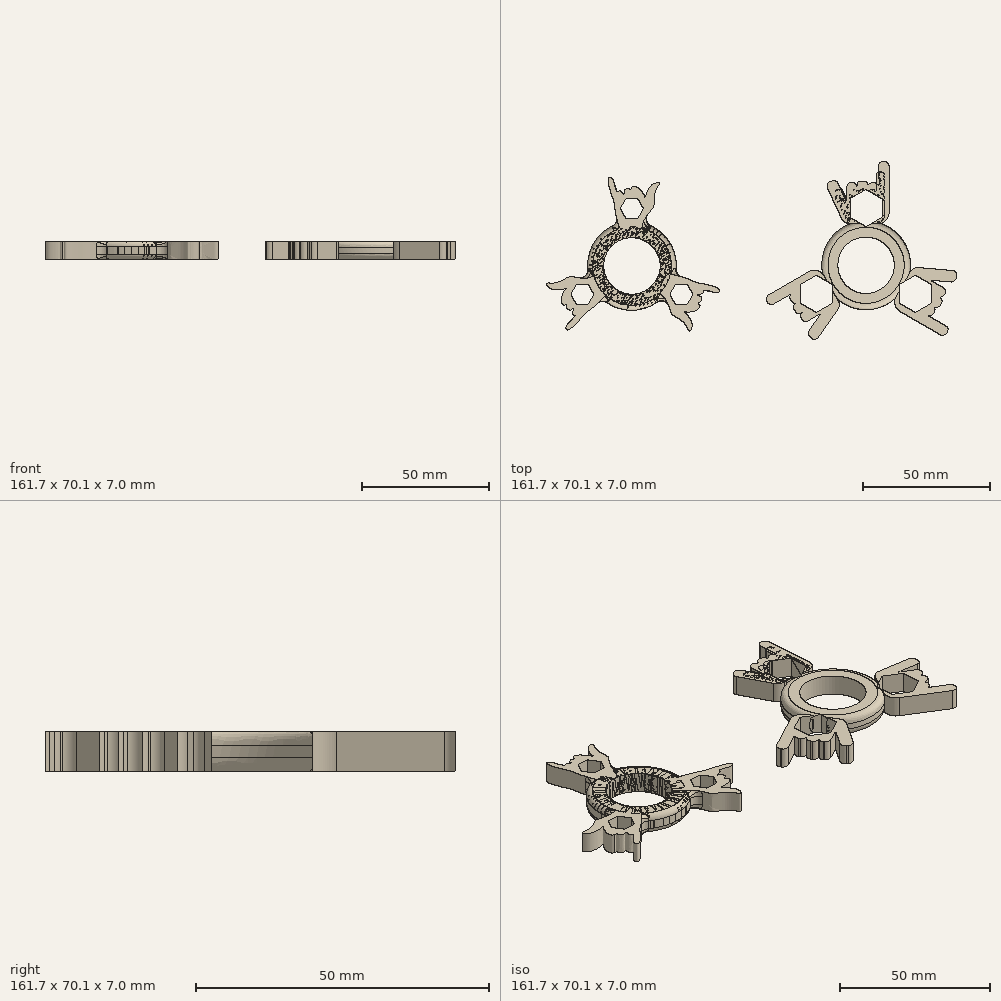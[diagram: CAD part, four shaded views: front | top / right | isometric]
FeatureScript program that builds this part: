
annotation { "Feature Type Name" : "Feature", "Feature Type Description" : "" }
export const myFeature = defineFeature(function(context is Context, id is Id, definition is map)
    precondition{}
    {
        {
            var Q0;
            Q0=qCreatedBy(makeId("Top.planeOp"),FACE);
            var sketch = newSketch(context, id + "F0", { "sketchPlane" : qUnion([Q0])});
            skPoint(sketch, "E0", {"position": v(0, 14) * mm});
            skPoint(sketch, "E1", {"position": v(0, 11.12) * mm});
            skLineSegment(sketch, "E2", {"start": v(-11.75, 14) * mm, "end": v(11.75, 14) * mm});
            skLineSegment(sketch, "E3", {"start": v(0, 14) * mm, "end": v(11.75, 14) * mm});
            skLineSegment(sketch, "E4", {"start": v(-11.75, 14) * mm, "end": v(0, 14) * mm});
            skLineSegment(sketch, "E5", {"start": v(0, 0) * mm, "end": v(0, 40) * mm});
            skPoint(sketch, "E6.13.internal.snap0", {"position": v(5.87, 14) * mm});
            skFitSpline(sketch, "E6", {"points": [v(5.87, 14) * mm, v(4.83, 16.75) * mm, v(4.45, 19.91) * mm, v(7.38, 24.48) * mm, v(8.56, 26.16) * mm, v(8.76, 28.18) * mm, v(8.91, 30.79) * mm, v(9.87, 33.45) * mm, v(10.71, 34.83) * mm, v(10.77, 35.56) * mm, v(9.34, 35.54) * mm, v(7.98, 34.9) * mm, v(6.44, 32.88) * mm, v(5.87, 31.7) * mm, v(5.72, 31.37) * mm, v(5.26, 29.43) * mm, v(4.97, 30.58) * mm, v(3.64, 32.5) * mm, v(2.81, 33.48) * mm, v(1.13, 34.27) * mm, v(0.25, 34) * mm, v(-0.2, 33.59) * mm, v(-0.3, 32.84) * mm, v(-1.06, 33.34) * mm, v(-2.25, 33.15) * mm, v(-3.12, 32.31) * mm, v(-3, 31.03) * mm, v(-4.48, 32.43) * mm, v(-5.19, 32.37) * mm, v(-5.55, 32.22) * mm, v(-5.81, 31.95) * mm, v(-6.05, 32.54) * mm, v(-6.77, 34.35) * mm, v(-7.78, 37.38) * mm, v(-9.18, 37.45) * mm, v(-9.22, 34.9) * mm, v(-9.22, 34.9) * mm, v(-8.3, 31.7) * mm, v(-7.12, 28.19) * mm, v(-6.67, 24.78) * mm, v(-6.18, 22.23) * mm, v(-5.26, 19) * mm, v(-4.33, 17.17) * mm, v(-3.58, 15.28) * mm, v(-3.38, 13.9) * mm, v(-3.35, 14) * mm], "startDerivative": vector(-16.05, 41.1) * mm, "endDerivative": vector(-65.23, -174.75) * mm});
            skLineSegment(sketch, "E7", {"start": v(0, 40) * mm, "end": v(-11.75, 40) * mm});
            skLineSegment(sketch, "E8", {"start": v(-11.75, 40) * mm, "end": v(-11.75, 45.72) * mm});
            skPoint(sketch, "E9", {"position": v(-3.55, 14) * mm});
            skLineSegment(sketch, "E10", {"start": v(0, 14) * mm, "end": v(0, -8.25) * mm});
            skCircle(sketch, "E11", {"center": v(0, 2.87) * mm, "radius": 11.13 * mm});
            skCircle(sketch, "E12", {"center": v(0, 2.87) * mm, "radius": 17.5 * mm});
            skCircle(sketch, "E13.cCircle", {"center": v(0, 25.42) * mm, "radius": 3.97 * mm, "construction": true});
            skLineSegment(sketch, "E13.0", {"start": v(2.3, 21.45) * mm, "end": v(-2.3, 21.45) * mm});
            skLineSegment(sketch, "E13.1", {"start": v(-2.3, 21.45) * mm, "end": v(-4.58, 25.42) * mm});
            skLineSegment(sketch, "E13.2", {"start": v(-4.58, 25.42) * mm, "end": v(-2.3, 29.4) * mm});
            skLineSegment(sketch, "E13.3", {"start": v(-2.3, 29.4) * mm, "end": v(2.3, 29.4) * mm});
            skLineSegment(sketch, "E13.4", {"start": v(2.3, 29.4) * mm, "end": v(4.58, 25.42) * mm});
            skLineSegment(sketch, "E13.5", {"start": v(4.58, 25.42) * mm, "end": v(2.3, 21.45) * mm});
            skPoint(sketch, "E13.0.midPoint", {"position": v(0, 21.45) * mm});
            skLineSegment(sketch, "E14", {"start": v(0, 2.87) * mm, "end": v(-3.26, 2.87) * mm});
            skSolve(sketch);
        }
        {
            var Q0;
            Q0 = qSketchRegion(id + "F0", true);
            extrude(context, id + "F1", {"entities" : qUnion([Q0]), "depth" : 7 * mm, "offsetDistance" : 25 * mm});
        }
        {
            var Q0;
            Q0=qCreatedBy(makeId("Top.planeOp"),FACE);
            var sketch = newSketch(context, id + "F2", { "sketchPlane" : qUnion([Q0])});
            skPoint(sketch, "E15", {"position": v(92.33, 14.59) * mm});
            skLineSegment(sketch, "E16", {"start": v(92.33, 0.24) * mm, "end": v(92.33, 40.24) * mm});
            skLineSegment(sketch, "E17", {"start": v(92.33, 40.24) * mm, "end": v(80.58, 40.24) * mm});
            skLineSegment(sketch, "E18", {"start": v(80.58, 40.24) * mm, "end": v(80.58, 45.96) * mm});
            skLineSegment(sketch, "E19", {"start": v(92.33, 14.59) * mm, "end": v(92.33, -8.35) * mm});
            skCircle(sketch, "E20", {"center": v(92.33, 3.12) * mm, "radius": 11.13 * mm});
            skCircle(sketch, "E21", {"center": v(92.33, 3.12) * mm, "radius": 17.5 * mm});
            skCircle(sketch, "E22.cCircle", {"center": v(91.53, 25.67) * mm, "radius": 3.97 * mm, "construction": true});
            skPoint(sketch, "E22.0.midPoint", {"position": v(91.53, 21.7) * mm});
            skLineSegment(sketch, "E23.bottom", {"start": v(87.38, 33.03) * mm, "end": v(87.71, 33.03) * mm});
            skLineSegment(sketch, "E23.top", {"start": v(87.38, 24.01) * mm, "end": v(87.71, 24.01) * mm});
            skLineSegment(sketch, "E23.left", {"start": v(85.88, 31.53) * mm, "end": v(85.88, 25.51) * mm});
            skLineSegment(sketch, "E23.right", {"start": v(89.21, 31.53) * mm, "end": v(89.21, 25.51) * mm});
            skLineSegment(sketch, "E24.bottom", {"start": v(94.82, 33.03) * mm, "end": v(94.4, 33.03) * mm});
            skLineSegment(sketch, "E24.top", {"start": v(94.82, 24.53) * mm, "end": v(94.4, 24.53) * mm});
            skLineSegment(sketch, "E24.left", {"start": v(96.32, 31.53) * mm, "end": v(96.32, 26.03) * mm});
            skLineSegment(sketch, "E24.right", {"start": v(92.9, 31.53) * mm, "end": v(92.9, 26.03) * mm});
            skLineSegment(sketch, "E25", {"start": v(89.21, 32.08) * mm, "end": v(89.21, 33.03) * mm});
            skLineSegment(sketch, "E26", {"start": v(90.71, 33.58) * mm, "end": v(91.4, 33.58) * mm});
            skLineSegment(sketch, "E27", {"start": v(92.9, 33.03) * mm, "end": v(92.9, 32.08) * mm});
            skLineSegment(sketch, "E28", {"start": v(89.21, 24.18) * mm, "end": v(89.21, 24.01) * mm});
            skLineSegment(sketch, "E29", {"start": v(90.71, 22.68) * mm, "end": v(91.4, 22.68) * mm});
            skLineSegment(sketch, "E30", {"start": v(92.9, 24.18) * mm, "end": v(92.9, 24.53) * mm});
            skPoint(sketch, "E31.visualSharp", {"position": v(85.88, 24.01) * mm});
            skArc(sketch, "E31.filletArc", {"start": v(85.88, 25.51) * mm, "mid": v(86.32, 24.45) * mm, "end": v(87.38, 24.01) * mm});
            skPoint(sketch, "E32.visualSharp", {"position": v(89.21, 24.01) * mm});
            skArc(sketch, "E32.filletArc", {"start": v(87.71, 24.01) * mm, "mid": v(88.77, 24.45) * mm, "end": v(89.21, 25.51) * mm});
            skLineSegment(sketch, "E33", {"start": v(89.21, 24.01) * mm, "end": v(89.21, 25.51) * mm});
            skPoint(sketch, "E34.visualSharp", {"position": v(89.21, 22.68) * mm});
            skArc(sketch, "E34.filletArc", {"start": v(89.21, 24.18) * mm, "mid": v(89.65, 23.12) * mm, "end": v(90.71, 22.68) * mm});
            skPoint(sketch, "E35.visualSharp", {"position": v(92.9, 22.68) * mm});
            skArc(sketch, "E35.filletArc", {"start": v(91.4, 22.68) * mm, "mid": v(92.45, 23.12) * mm, "end": v(92.9, 24.18) * mm});
            skPoint(sketch, "E36.visualSharp", {"position": v(96.32, 24.53) * mm});
            skArc(sketch, "E36.filletArc", {"start": v(94.82, 24.53) * mm, "mid": v(95.88, 24.97) * mm, "end": v(96.32, 26.03) * mm});
            skPoint(sketch, "E37.visualSharp", {"position": v(96.32, 33.03) * mm});
            skArc(sketch, "E37.filletArc", {"start": v(96.32, 31.53) * mm, "mid": v(95.88, 32.6) * mm, "end": v(94.82, 33.03) * mm});
            skPoint(sketch, "E38.visualSharp", {"position": v(85.88, 33.03) * mm});
            skArc(sketch, "E38.filletArc", {"start": v(87.38, 33.03) * mm, "mid": v(86.32, 32.6) * mm, "end": v(85.88, 31.53) * mm});
            skPoint(sketch, "E39.visualSharp", {"position": v(89.21, 33.58) * mm});
            skArc(sketch, "E39.filletArc", {"start": v(90.71, 33.58) * mm, "mid": v(89.65, 33.14) * mm, "end": v(89.21, 32.08) * mm});
            skPoint(sketch, "E40.visualSharp", {"position": v(92.9, 33.58) * mm});
            skArc(sketch, "E40.filletArc", {"start": v(92.9, 32.08) * mm, "mid": v(92.45, 33.14) * mm, "end": v(91.4, 33.58) * mm});
            skPoint(sketch, "E41.visualSharp", {"position": v(92.9, 33.03) * mm});
            skArc(sketch, "E41.filletArc", {"start": v(94.4, 33.03) * mm, "mid": v(93.33, 32.6) * mm, "end": v(92.9, 31.53) * mm});
            skPoint(sketch, "E42.visualSharp", {"position": v(92.9, 24.53) * mm});
            skArc(sketch, "E42.filletArc", {"start": v(92.9, 26.03) * mm, "mid": v(93.33, 24.97) * mm, "end": v(94.4, 24.53) * mm});
            skPoint(sketch, "E43.visualSharp", {"position": v(89.21, 33.03) * mm});
            skArc(sketch, "E43.filletArc", {"start": v(89.21, 31.53) * mm, "mid": v(88.77, 32.6) * mm, "end": v(87.71, 33.03) * mm});
            skLineSegment(sketch, "E44", {"start": v(92.9, 24.53) * mm, "end": v(92.9, 26.03) * mm});
            skLineSegment(sketch, "E45", {"start": v(89.21, 31.53) * mm, "end": v(89.21, 32.08) * mm});
            skLineSegment(sketch, "E46", {"start": v(92.9, 32.08) * mm, "end": v(92.9, 31.53) * mm});
            skLineSegment(sketch, "E47", {"start": v(96.32, 31.53) * mm, "end": v(96.32, 38.48) * mm});
            skLineSegment(sketch, "E48", {"start": v(97.82, 39.98) * mm, "end": v(98.15, 39.98) * mm});
            skLineSegment(sketch, "E49", {"start": v(99.75, 38.38) * mm, "end": v(99.75, 23.09) * mm});
            skLineSegment(sketch, "E50", {"start": v(96.25, 19.59) * mm, "end": v(86.83, 19.59) * mm});
            skLineSegment(sketch, "E51", {"start": v(84.1, 21.32) * mm, "end": v(79.49, 31.22) * mm});
            skLineSegment(sketch, "E52", {"start": v(80.21, 33.22) * mm, "end": v(80.94, 33.56) * mm});
            skLineSegment(sketch, "E53", {"start": v(82.93, 32.83) * mm, "end": v(85.88, 26.52) * mm});
            skPoint(sketch, "E54.visualSharp", {"position": v(82.3, 34.19) * mm});
            skArc(sketch, "E54.filletArc", {"start": v(82.93, 32.83) * mm, "mid": v(82.09, 33.6) * mm, "end": v(80.94, 33.56) * mm});
            skPoint(sketch, "E55.visualSharp", {"position": v(78.85, 32.58) * mm});
            skArc(sketch, "E55.filletArc", {"start": v(80.21, 33.22) * mm, "mid": v(79.44, 32.37) * mm, "end": v(79.49, 31.22) * mm});
            skPoint(sketch, "E56.visualSharp", {"position": v(96.32, 39.98) * mm});
            skArc(sketch, "E56.filletArc", {"start": v(97.82, 39.98) * mm, "mid": v(96.76, 39.54) * mm, "end": v(96.32, 38.48) * mm});
            skPoint(sketch, "E57.visualSharp", {"position": v(99.75, 39.98) * mm});
            skArc(sketch, "E57.filletArc", {"start": v(99.75, 38.38) * mm, "mid": v(99.29, 39.51) * mm, "end": v(98.15, 39.98) * mm});
            skPoint(sketch, "E58.visualSharp", {"position": v(84.91, 19.59) * mm});
            skArc(sketch, "E58.filletArc", {"start": v(84.1, 21.32) * mm, "mid": v(85.21, 20.06) * mm, "end": v(86.83, 19.59) * mm});
            skPoint(sketch, "E59.visualSharp", {"position": v(99.75, 19.59) * mm});
            skArc(sketch, "E59.filletArc", {"start": v(96.25, 19.59) * mm, "mid": v(98.73, 20.61) * mm, "end": v(99.75, 23.09) * mm});
            skFitSpline(sketch, "E60", {"points": [v(178.18, -38.8) * mm, v(177.13, -36.06) * mm, v(176.76, -32.89) * mm, v(179.68, -28.32) * mm, v(180.87, -26.64) * mm, v(181.07, -24.63) * mm, v(181.22, -22.01) * mm, v(182.17, -19.35) * mm, v(183.02, -17.98) * mm, v(183.08, -17.24) * mm, v(181.64, -17.26) * mm, v(180.29, -17.9) * mm, v(178.74, -19.92) * mm, v(178.18, -21.1) * mm, v(178.02, -21.43) * mm, v(177.56, -23.37) * mm, v(177.27, -22.22) * mm, v(175.95, -20.3) * mm, v(175.11, -19.33) * mm, v(173.43, -18.53) * mm, v(172.56, -18.8) * mm, v(172.1, -19.21) * mm, v(172, -19.96) * mm, v(171.25, -19.46) * mm, v(170.05, -19.65) * mm, v(169.18, -20.49) * mm, v(169.31, -21.78) * mm, v(167.82, -20.37) * mm, v(167.11, -20.43) * mm, v(166.75, -20.58) * mm, v(166.49, -20.86) * mm, v(166.26, -20.26) * mm, v(165.54, -18.45) * mm, v(164.53, -15.43) * mm, v(163.13, -15.35) * mm, v(163.09, -17.9) * mm, v(163.09, -17.9) * mm, v(164, -21.1) * mm, v(165.18, -24.61) * mm, v(165.64, -28.02) * mm, v(166.13, -30.57) * mm, v(167.04, -33.8) * mm, v(167.98, -35.63) * mm, v(168.72, -37.52) * mm, v(168.92, -38.91) * mm, v(168.96, -38.8) * mm], "startDerivative": vector(-16.05, 41.1) * mm, "endDerivative": vector(-65.23, -174.75) * mm});
            skPoint(sketch, "E61", {"position": v(91.54, 19.59) * mm});
            skLineSegment(sketch, "E62", {"start": v(92.33, 14.59) * mm, "end": v(92.33, 19.59) * mm});
            skLineSegment(sketch, "E63", {"start": v(92.33, 3.12) * mm, "end": v(94.68, 3.12) * mm});
            skCircle(sketch, "E64", {"center": v(92.33, 3.12) * mm, "radius": 11.12 * mm});
            skCircle(sketch, "E65", {"center": v(92.33, 3.12) * mm, "radius": 12 * mm});
            skSolve(sketch);
        }
        {
            var Q0;
            Q0=makeQuery(id+"F2.imprint","IMPRINT",FACE,{"disambiguationData":[TD([[makeQuery(id+"F2.imprint","IMPRINT",EDGE,{"derivedFrom":sQuery(id+"F2.wireOp",EDGE,"E23.top")}),-1.0]])]});
            var Q1;
            Q1=makeQuery(id+"F2.imprint","IMPRINT",FACE,{"disambiguationData":[TD([[makeQuery(id+"F2.imprint","IMPRINT",EDGE,{"derivedFrom":sQuery(id+"F2.wireOp",EDGE,"E23.bottom")}),-1.0]])]});
            var Q2;
            {var subQ0=sQuery(id+"F2.wireOp",EDGE,"E22.2");var subQ1=sQuery(id+"F2.wireOp",EDGE,"E22.1");var subQ2=makeQuery(id+"F2.imprint","INTERSECT",VERTEX,{"derivedFrom":[subQ1,subQ0]});Q2=makeQuery(id+"F2.imprint","IMPRINT",FACE,{"disambiguationData":[TD([[makeQuery(id+"F2.imprint","IMPRINT",EDGE,{"disambiguationData":[TD([[subQ2,1.0]])],"derivedFrom":subQ1}),-1.0]])]});}
            var Q3;
            {var subQ8=sQuery(id+"F2.wireOp",EDGE,"E26");Q3=makeQuery(id+"F2.imprint","IMPRINT",FACE,{"disambiguationData":[TD([[makeQuery(id+"F2.imprint","IMPRINT",EDGE,{"derivedFrom":subQ8}),-1.0]])]});}
            var Q4;
            {var subQ0=sQuery(id+"F2.wireOp",EDGE,"E46");Q4=makeQuery(id+"F2.imprint","IMPRINT",FACE,{"disambiguationData":[TD([[makeQuery(id+"F2.imprint","IMPRINT",EDGE,{"derivedFrom":subQ0}),-1.0]])]});}
            var Q5;
            {var subQ9=sQuery(id+"F2.wireOp",EDGE,"E29");Q5=makeQuery(id+"F2.imprint","IMPRINT",FACE,{"disambiguationData":[TD([[makeQuery(id+"F2.imprint","IMPRINT",EDGE,{"derivedFrom":subQ9}),1.0]])]});}
            var Q6;
            {var subQ0=sQuery(id+"F2.wireOp",EDGE,"E30");Q6=makeQuery(id+"F2.imprint","IMPRINT",FACE,{"disambiguationData":[TD([[makeQuery(id+"F2.imprint","IMPRINT",EDGE,{"derivedFrom":subQ0}),1.0]])]});}
            var Q7;
            {var subQ1=sQuery(id+"F2.wireOp",EDGE,"E22.4");Q7=makeQuery(id+"F2.imprint","IMPRINT",FACE,{"disambiguationData":[TD([[makeQuery(id+"F2.imprint","IMPRINT",EDGE,{"derivedFrom":subQ1}),-1.0]])]});}
            var Q8;
            {var subQ2=sQuery(id+"F2.wireOp",EDGE,"E22.4");Q8=makeQuery(id+"F2.imprint","IMPRINT",FACE,{"disambiguationData":[TD([[makeQuery(id+"F2.imprint","IMPRINT",EDGE,{"derivedFrom":subQ2}),1.0]])]});}
            var Q9;
            {var subQ1=sQuery(id+"F2.wireOp",EDGE,"E24.left");Q9=makeQuery(id+"F2.imprint","IMPRINT",FACE,{"disambiguationData":[TD([[makeQuery(id+"F2.imprint","IMPRINT",EDGE,{"derivedFrom":subQ1}),1.0]])]});}
            var Q10;
            {var subQ0=sQuery(id+"F2.wireOp",EDGE,"E24.top");Q10=makeQuery(id+"F2.imprint","IMPRINT",FACE,{"disambiguationData":[TD([[makeQuery(id+"F2.imprint","IMPRINT",EDGE,{"derivedFrom":subQ0}),1.0]])]});}
            var Q11;
            {var subQ0=sQuery(id+"F2.wireOp",EDGE,"E29");Q11=makeQuery(id+"F2.imprint","IMPRINT",FACE,{"disambiguationData":[TD([[makeQuery(id+"F2.imprint","IMPRINT",EDGE,{"derivedFrom":subQ0}),-1.0]])]});}
            var Q12;
            {var subQ0=sQuery(id+"F2.wireOp",EDGE,"E50");var subQ1=sQuery(id+"F2.wireOp",EDGE,"E16");var subQ2=makeQuery(id+"F2.imprint","INTERSECT",VERTEX,{"derivedFrom":[subQ1,subQ0]});Q12=makeQuery(id+"F2.imprint","IMPRINT",FACE,{"disambiguationData":[TD([[makeQuery(id+"F2.imprint","IMPRINT",EDGE,{"disambiguationData":[TD([[subQ2,-1.0]])],"derivedFrom":subQ1}),1.0]])]});}
            var Q13;
            {var subQ0=sQuery(id+"F2.wireOp",EDGE,"E50");var subQ1=sQuery(id+"F2.wireOp",EDGE,"E16");var subQ2=makeQuery(id+"F2.imprint","INTERSECT",VERTEX,{"derivedFrom":[subQ1,subQ0]});Q13=makeQuery(id+"F2.imprint","IMPRINT",FACE,{"disambiguationData":[TD([[makeQuery(id+"F2.imprint","IMPRINT",EDGE,{"disambiguationData":[TD([[subQ2,-1.0]])],"derivedFrom":subQ1}),-1.0]])]});}
            var Q14;
            Q14=makeQuery(id+"F2.imprint","IMPRINT",FACE,{"disambiguationData":[TD([[makeQuery(id+"F2.imprint","IMPRINT",EDGE,{"derivedFrom":sQuery(id+"F2.wireOp",EDGE,"E24.bottom")}),1.0]])]});
            extrude(context, id + "F3", {"entities" : qUnion([Q0, Q1, Q2, Q3, Q4, Q5, Q6, Q7, Q8, Q9, Q10, Q11, Q12, Q13, Q14]), "depth" : 7 * mm, "offsetDistance" : 25 * mm});
        }
        {
            var Q0;
            Q0=makeQuery(id+"F2.imprint","IMPRINT",FACE,{"disambiguationData":[TD([[makeQuery(id+"F2.imprint","IMPRINT",EDGE,{"derivedFrom":sQuery(id+"F2.wireOp",EDGE,"E65")}),-1.0]])]});
            var Q1;
            Q1=makeQuery(id+"F2.imprint","IMPRINT",FACE,{"disambiguationData":[TD([[makeQuery(id+"F2.imprint","IMPRINT",EDGE,{"derivedFrom":sQuery(id+"F2.wireOp",EDGE,"E65")}),1.0]])]});
            extrude(context, id + "F4", {"entities" : qUnion([Q0, Q1]), "depth" : 7 * mm, "offsetDistance" : 25 * mm});
        }
        {
            var Q0;
            Q0=makeQuery(id+"F4.opExtrude","CAP_EDGE",EDGE,{"disambiguationData":[OSD([sQuery(id+"F2.wireOp",EDGE,"E21")])],"isStart":false});
            var Q1;
            Q1=makeQuery(id+"F4.opExtrude","CAP_EDGE",EDGE,{"disambiguationData":[OSD([sQuery(id+"F2.wireOp",EDGE,"E21")])],"isStart":true});
            fillet(context, id + "F5", {"entities" : qUnion([Q0, Q1]), "radius" : 2.5 * mm, "tangentPropagation" : true, "rho" : 0.5, "crossSection" : FilletCrossSection.CONIC, "allowEdgeOverflow" : false});
        }
        {
            var Q0;
            {var subQ1=sQuery(id+"F0.wireOp",EDGE,"E10");var subQ3=makeQuery(id+"F0.imprint","IMPRINT",VERTEX,{"disambiguationData":[OD(0.0)],"derivedFrom":subQ1});Q0=makeQuery(id+"F0.imprint","IMPRINT",FACE,{"disambiguationData":[TD([[makeQuery(id+"F0.imprint","IMPRINT",EDGE,{"disambiguationData":[TD([[subQ3,-1.0]])],"derivedFrom":subQ1}),-1.0]])]});}
            var Q1;
            Q1=sQuery(id+"F0.wireOp",EDGE,"E14");
            extrude(context, id + "F6", {"entities" : qUnion([Q0]), "bodyType" : ExtendedToolBodyType.SURFACE, "surfaceEntities" : qUnion([Q1]), "depth" : 25 * mm, "offsetDistance" : 25 * mm});
        }
        {
            var Q0;
            Q0=makeQuery(id+"F1.opExtrude","CAP_EDGE",EDGE,{"disambiguationData":[OSD([sQuery(id+"F0.wireOp",EDGE,"E12")])],"isStart":false});
            var Q1;
            Q1=makeQuery(id+"F1.opExtrude","CAP_EDGE",EDGE,{"disambiguationData":[OSD([sQuery(id+"F0.wireOp",EDGE,"E12")])],"isStart":true});
            fillet(context, id + "F7", {"entities" : qUnion([Q0, Q1]), "radius" : 2 * mm, "tangentPropagation" : true, "allowEdgeOverflow" : false});
        }
        {
            var Q0;
            {var subQ0=sQuery(id+"F0.wireOp",EDGE,"E12");var subQ1=sQuery(id+"F0.wireOp",EDGE,"E6");Q0=makeQuery(id+"F1.opExtrude","SWEPT_EDGE",EDGE,{"disambiguationData":[OSD([subQ1,subQ0]),TDD([makeQuery(id+"F0.imprint","INTERSECT",VERTEX,{"disambiguationData":[OD(0.0)],"derivedFrom":[subQ1,subQ0]})])]});}
            var Q1;
            {var subQ0=sQuery(id+"F0.wireOp",EDGE,"E12");var subQ1=sQuery(id+"F0.wireOp",EDGE,"E6");Q1=makeQuery(id+"F1.opExtrude","SWEPT_EDGE",EDGE,{"disambiguationData":[OSD([subQ1,subQ0]),TDD([makeQuery(id+"F0.imprint","INTERSECT",VERTEX,{"disambiguationData":[OD(1.0)],"derivedFrom":[subQ1,subQ0]})])]});}
            fillet(context, id + "F8", {"entities" : qUnion([Q0, Q1]), "radius" : 3 * mm, "tangentPropagation" : true, "allowEdgeOverflow" : false});
        }
        {
            var Q0;
            Q0=qCreatedBy(makeId("Top.planeOp"),FACE);
            var sketch = newSketch(context, id + "F9", { "sketchPlane" : qUnion([Q0])});
            skLineSegment(sketch, "E66", {"start": v(92.33, 3.12) * mm, "end": v(92.33, 25.67) * mm});
            skCircle(sketch, "E67.cCircle", {"center": v(92.33, 25.67) * mm, "radius": 7.33 * mm, "construction": true});
            skLineSegment(sketch, "E67.0", {"start": v(92.33, 18.33) * mm, "end": v(85.98, 22) * mm});
            skLineSegment(sketch, "E67.1", {"start": v(85.98, 22) * mm, "end": v(85.98, 29.33) * mm});
            skLineSegment(sketch, "E67.2", {"start": v(85.98, 29.33) * mm, "end": v(92.33, 33) * mm});
            skLineSegment(sketch, "E67.3", {"start": v(92.33, 33) * mm, "end": v(98.68, 29.33) * mm});
            skLineSegment(sketch, "E67.4", {"start": v(98.68, 29.33) * mm, "end": v(98.68, 22) * mm});
            skLineSegment(sketch, "E67.5", {"start": v(98.68, 22) * mm, "end": v(92.33, 18.33) * mm});
            skLineSegment(sketch, "E68.1.0", {"start": v(79.15, -4.49) * mm, "end": v(79.15, -11.82) * mm});
            skLineSegment(sketch, "E68.1.1", {"start": v(79.15, -11.82) * mm, "end": v(72.8, -15.49) * mm});
            skLineSegment(sketch, "E68.1.2", {"start": v(72.8, -15.49) * mm, "end": v(66.45, -11.82) * mm});
            skLineSegment(sketch, "E68.1.3", {"start": v(66.45, -11.82) * mm, "end": v(66.45, -4.49) * mm});
            skLineSegment(sketch, "E68.1.4", {"start": v(66.45, -4.49) * mm, "end": v(72.8, -0.82) * mm});
            skLineSegment(sketch, "E68.1.5", {"start": v(72.8, -0.82) * mm, "end": v(79.15, -4.49) * mm});
            skLineSegment(sketch, "E68.2.0", {"start": v(105.5, -4.49) * mm, "end": v(111.85, -0.82) * mm});
            skLineSegment(sketch, "E68.2.1", {"start": v(111.85, -0.82) * mm, "end": v(118.2, -4.49) * mm});
            skLineSegment(sketch, "E68.2.2", {"start": v(118.2, -4.49) * mm, "end": v(118.2, -11.82) * mm});
            skLineSegment(sketch, "E68.2.3", {"start": v(118.2, -11.82) * mm, "end": v(111.85, -15.49) * mm});
            skLineSegment(sketch, "E68.2.4", {"start": v(111.85, -15.49) * mm, "end": v(105.5, -11.82) * mm});
            skLineSegment(sketch, "E68.2.5", {"start": v(105.5, -11.82) * mm, "end": v(105.5, -4.49) * mm});
            skPoint(sketch, "E68.center", {"position": v(92.33, 3.12) * mm});
            skSolve(sketch);
        }
        {
            var Q0;
            Q0=makeQuery(id+"F1.opExtrude","SWEPT_BODY",BODY,{"disambiguationData":[OSD([sQuery(id+"F0.wireOp",EDGE,"E6"),sQuery(id+"F0.wireOp",EDGE,"E11"),sQuery(id+"F0.wireOp",EDGE,"E12"),sQuery(id+"F0.wireOp",EDGE,"E13.0"),sQuery(id+"F0.wireOp",EDGE,"E13.1"),sQuery(id+"F0.wireOp",EDGE,"E13.2"),sQuery(id+"F0.wireOp",EDGE,"E13.3"),sQuery(id+"F0.wireOp",EDGE,"E13.4"),sQuery(id+"F0.wireOp",EDGE,"E13.5")])]});
            var Q1;
            Q1=makeQuery(id+"F6.opExtrude","SWEPT_EDGE",EDGE,{"disambiguationData":[OSD([sQuery(id+"F0.wireOp",VERTEX,"E14.start")])]});
            circularPattern(context, id + "F10", {"operationType" : NewBodyOperationType.ADD, "entities" : qUnion([Q0]), "axis" : qUnion([Q1]), "angle" : 360 * degree, "instanceCount" : 3, "equalSpace" : true, "computeTransformsWithoutBuiltin" : true});
        }
        {
            var Q0;
            Q0=sQuery(id+"F2.wireOp",EDGE,"E63");
            extrude(context, id + "F11", {"bodyType" : ExtendedToolBodyType.SURFACE, "surfaceEntities" : qUnion([Q0]), "depth" : 5 * mm, "offsetDistance" : 25 * mm});
        }
        {
            var Q0;
            Q0=makeQuery(id+"F3.opExtrude","SWEPT_BODY",BODY,{"disambiguationData":[OSD([sQuery(id+"F2.wireOp",EDGE,"E23.bottom"),sQuery(id+"F2.wireOp",EDGE,"E23.left"),sQuery(id+"F2.wireOp",EDGE,"E24.bottom"),sQuery(id+"F2.wireOp",EDGE,"E26"),sQuery(id+"F2.wireOp",EDGE,"E37.filletArc"),sQuery(id+"F2.wireOp",EDGE,"E38.filletArc"),sQuery(id+"F2.wireOp",EDGE,"E39.filletArc"),sQuery(id+"F2.wireOp",EDGE,"E40.filletArc"),sQuery(id+"F2.wireOp",EDGE,"E41.filletArc"),sQuery(id+"F2.wireOp",EDGE,"E43.filletArc"),sQuery(id+"F2.wireOp",EDGE,"E45"),sQuery(id+"F2.wireOp",EDGE,"E46"),sQuery(id+"F2.wireOp",EDGE,"E47"),sQuery(id+"F2.wireOp",EDGE,"E48"),sQuery(id+"F2.wireOp",EDGE,"E49"),sQuery(id+"F2.wireOp",EDGE,"E50"),sQuery(id+"F2.wireOp",EDGE,"E51"),sQuery(id+"F2.wireOp",EDGE,"E52"),sQuery(id+"F2.wireOp",EDGE,"E53"),sQuery(id+"F2.wireOp",EDGE,"E54.filletArc"),sQuery(id+"F2.wireOp",EDGE,"E55.filletArc"),sQuery(id+"F2.wireOp",EDGE,"E56.filletArc"),sQuery(id+"F2.wireOp",EDGE,"E57.filletArc"),sQuery(id+"F2.wireOp",EDGE,"E58.filletArc"),sQuery(id+"F2.wireOp",EDGE,"E59.filletArc")])]});
            var Q1;
            Q1=sQuery(id+"F2.wireOp",VERTEX,"E61");
            transform(context, id + "F12", {"entities" : qUnion([Q0]), "transformType" : TransformType.SCALE_UNIFORMLY, "scale" : 1.2, "scalePoint" : qUnion([Q1]), "makeCopy" : true});
        }
        {
            var Q0;
            Q0=makeQuery(id+"F12.opPattern","COPY",BODY,{"derivedFrom":makeQuery(id+"F3.opExtrude","SWEPT_BODY",BODY,{"disambiguationData":[OSD([sQuery(id+"F2.wireOp",EDGE,"E23.bottom"),sQuery(id+"F2.wireOp",EDGE,"E23.left"),sQuery(id+"F2.wireOp",EDGE,"E24.bottom"),sQuery(id+"F2.wireOp",EDGE,"E26"),sQuery(id+"F2.wireOp",EDGE,"E37.filletArc"),sQuery(id+"F2.wireOp",EDGE,"E38.filletArc"),sQuery(id+"F2.wireOp",EDGE,"E39.filletArc"),sQuery(id+"F2.wireOp",EDGE,"E40.filletArc"),sQuery(id+"F2.wireOp",EDGE,"E41.filletArc"),sQuery(id+"F2.wireOp",EDGE,"E43.filletArc"),sQuery(id+"F2.wireOp",EDGE,"E45"),sQuery(id+"F2.wireOp",EDGE,"E46"),sQuery(id+"F2.wireOp",EDGE,"E47"),sQuery(id+"F2.wireOp",EDGE,"E48"),sQuery(id+"F2.wireOp",EDGE,"E49"),sQuery(id+"F2.wireOp",EDGE,"E50"),sQuery(id+"F2.wireOp",EDGE,"E51"),sQuery(id+"F2.wireOp",EDGE,"E52"),sQuery(id+"F2.wireOp",EDGE,"E53"),sQuery(id+"F2.wireOp",EDGE,"E54.filletArc"),sQuery(id+"F2.wireOp",EDGE,"E55.filletArc"),sQuery(id+"F2.wireOp",EDGE,"E56.filletArc"),sQuery(id+"F2.wireOp",EDGE,"E57.filletArc"),sQuery(id+"F2.wireOp",EDGE,"E58.filletArc"),sQuery(id+"F2.wireOp",EDGE,"E59.filletArc")])]}),"instanceName":"1"});
            var Q1;
            Q1=makeQuery(id+"F11.opExtrude","SWEPT_EDGE",EDGE,{"disambiguationData":[OSD([sQuery(id+"F2.wireOp",VERTEX,"E63.start")])]});
            circularPattern(context, id + "F13", {"entities" : qUnion([Q0]), "axis" : qUnion([Q1]), "angle" : 360 * degree, "instanceCount" : 3, "equalSpace" : true, "computeTransformsWithoutBuiltin" : true});
        }
        {
            var Q0;
            Q0 = qSketchRegion(id + "F9", true);
            extrude(context, id + "F14", {"entities" : qUnion([Q0]), "operationType" : NewBodyOperationType.REMOVE, "depth" : 25 * mm, "offsetDistance" : 25 * mm});
        }
        {
            var Q0;
            Q0=makeQuery(id+"F12.opPattern","COPY",FACE,{"derivedFrom":makeQuery(id+"F3.opExtrude","CAP_FACE",FACE,{"disambiguationData":[OSD([sQuery(id+"F2.wireOp",EDGE,"E23.bottom"),sQuery(id+"F2.wireOp",EDGE,"E23.left"),sQuery(id+"F2.wireOp",EDGE,"E24.bottom"),sQuery(id+"F2.wireOp",EDGE,"E26"),sQuery(id+"F2.wireOp",EDGE,"E37.filletArc"),sQuery(id+"F2.wireOp",EDGE,"E38.filletArc"),sQuery(id+"F2.wireOp",EDGE,"E39.filletArc"),sQuery(id+"F2.wireOp",EDGE,"E40.filletArc"),sQuery(id+"F2.wireOp",EDGE,"E41.filletArc"),sQuery(id+"F2.wireOp",EDGE,"E43.filletArc"),sQuery(id+"F2.wireOp",EDGE,"E45"),sQuery(id+"F2.wireOp",EDGE,"E46"),sQuery(id+"F2.wireOp",EDGE,"E47"),sQuery(id+"F2.wireOp",EDGE,"E48"),sQuery(id+"F2.wireOp",EDGE,"E49"),sQuery(id+"F2.wireOp",EDGE,"E50"),sQuery(id+"F2.wireOp",EDGE,"E51"),sQuery(id+"F2.wireOp",EDGE,"E52"),sQuery(id+"F2.wireOp",EDGE,"E53"),sQuery(id+"F2.wireOp",EDGE,"E54.filletArc"),sQuery(id+"F2.wireOp",EDGE,"E55.filletArc"),sQuery(id+"F2.wireOp",EDGE,"E56.filletArc"),sQuery(id+"F2.wireOp",EDGE,"E57.filletArc"),sQuery(id+"F2.wireOp",EDGE,"E58.filletArc"),sQuery(id+"F2.wireOp",EDGE,"E59.filletArc")])],"isStart":false}),"instanceName":"1"});
            var Q1;
            Q1=makeQuery(id+"F13.opPattern","COPY",FACE,{"derivedFrom":makeQuery(id+"F12.opPattern","COPY",FACE,{"derivedFrom":makeQuery(id+"F3.opExtrude","CAP_FACE",FACE,{"disambiguationData":[OSD([sQuery(id+"F2.wireOp",EDGE,"E23.bottom"),sQuery(id+"F2.wireOp",EDGE,"E23.left"),sQuery(id+"F2.wireOp",EDGE,"E24.bottom"),sQuery(id+"F2.wireOp",EDGE,"E26"),sQuery(id+"F2.wireOp",EDGE,"E37.filletArc"),sQuery(id+"F2.wireOp",EDGE,"E38.filletArc"),sQuery(id+"F2.wireOp",EDGE,"E39.filletArc"),sQuery(id+"F2.wireOp",EDGE,"E40.filletArc"),sQuery(id+"F2.wireOp",EDGE,"E41.filletArc"),sQuery(id+"F2.wireOp",EDGE,"E43.filletArc"),sQuery(id+"F2.wireOp",EDGE,"E45"),sQuery(id+"F2.wireOp",EDGE,"E46"),sQuery(id+"F2.wireOp",EDGE,"E47"),sQuery(id+"F2.wireOp",EDGE,"E48"),sQuery(id+"F2.wireOp",EDGE,"E49"),sQuery(id+"F2.wireOp",EDGE,"E50"),sQuery(id+"F2.wireOp",EDGE,"E51"),sQuery(id+"F2.wireOp",EDGE,"E52"),sQuery(id+"F2.wireOp",EDGE,"E53"),sQuery(id+"F2.wireOp",EDGE,"E54.filletArc"),sQuery(id+"F2.wireOp",EDGE,"E55.filletArc"),sQuery(id+"F2.wireOp",EDGE,"E56.filletArc"),sQuery(id+"F2.wireOp",EDGE,"E57.filletArc"),sQuery(id+"F2.wireOp",EDGE,"E58.filletArc"),sQuery(id+"F2.wireOp",EDGE,"E59.filletArc")])],"isStart":false}),"instanceName":"1"}),"instanceName":"2"});
            var Q2;
            Q2=makeQuery(id+"F13.opPattern","COPY",FACE,{"derivedFrom":makeQuery(id+"F12.opPattern","COPY",FACE,{"derivedFrom":makeQuery(id+"F3.opExtrude","CAP_FACE",FACE,{"disambiguationData":[OSD([sQuery(id+"F2.wireOp",EDGE,"E23.bottom"),sQuery(id+"F2.wireOp",EDGE,"E23.left"),sQuery(id+"F2.wireOp",EDGE,"E24.bottom"),sQuery(id+"F2.wireOp",EDGE,"E26"),sQuery(id+"F2.wireOp",EDGE,"E37.filletArc"),sQuery(id+"F2.wireOp",EDGE,"E38.filletArc"),sQuery(id+"F2.wireOp",EDGE,"E39.filletArc"),sQuery(id+"F2.wireOp",EDGE,"E40.filletArc"),sQuery(id+"F2.wireOp",EDGE,"E41.filletArc"),sQuery(id+"F2.wireOp",EDGE,"E43.filletArc"),sQuery(id+"F2.wireOp",EDGE,"E45"),sQuery(id+"F2.wireOp",EDGE,"E46"),sQuery(id+"F2.wireOp",EDGE,"E47"),sQuery(id+"F2.wireOp",EDGE,"E48"),sQuery(id+"F2.wireOp",EDGE,"E49"),sQuery(id+"F2.wireOp",EDGE,"E50"),sQuery(id+"F2.wireOp",EDGE,"E51"),sQuery(id+"F2.wireOp",EDGE,"E52"),sQuery(id+"F2.wireOp",EDGE,"E53"),sQuery(id+"F2.wireOp",EDGE,"E54.filletArc"),sQuery(id+"F2.wireOp",EDGE,"E55.filletArc"),sQuery(id+"F2.wireOp",EDGE,"E56.filletArc"),sQuery(id+"F2.wireOp",EDGE,"E57.filletArc"),sQuery(id+"F2.wireOp",EDGE,"E58.filletArc"),sQuery(id+"F2.wireOp",EDGE,"E59.filletArc")])],"isStart":false}),"instanceName":"1"}),"instanceName":"1"});
            extrude(context, id + "F15", {"entities" : qUnion([Q0, Q1, Q2]), "operationType" : NewBodyOperationType.REMOVE, "oppositeDirection" : true, "depth" : 1.4 * mm, "offsetDistance" : 25 * mm});
        }
    });
